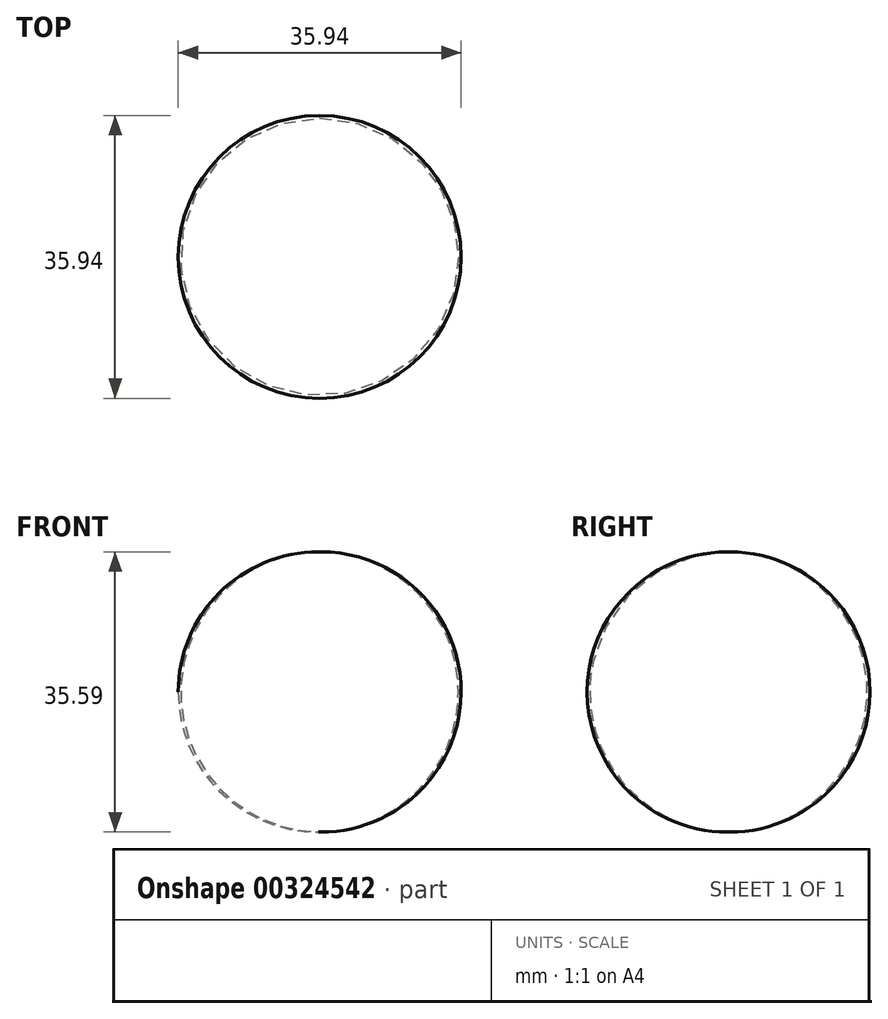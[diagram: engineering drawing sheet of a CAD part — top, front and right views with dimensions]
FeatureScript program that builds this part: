
annotation { "Feature Type Name" : "Feature", "Feature Type Description" : "" }
export const myFeature = defineFeature(function(context is Context, id is Id, definition is map)
    precondition{}
    {
        {
            var Q0;
            Q0=qCreatedBy(makeId("Front.planeOp"),FACE);
            var sketch = newSketch(context, id + "F0", { "sketchPlane" : qUnion([Q0])});
            skArc(sketch, "E0", {"start": v(0, -35.6) * mm, "mid": v(17.63, -17.8) * mm, "end": v(0, 0) * mm});
            skLineSegment(sketch, "E1", {"start": v(0, 0) * mm, "end": v(0, -35.6) * mm});
            skLineSegment(sketch, "E2", {"start": v(0, -59.1) * mm, "end": v(0, 28.13) * mm, "construction": true});
            skSolve(sketch);
        }
        {
            var Q0;
            Q0=makeQuery(id+"F0.imprint","IMPRINT",FACE,{"disambiguationData":[TD([[makeQuery(id+"F0.imprint","IMPRINT",EDGE,{"derivedFrom":sQuery(id+"F0.wireOp",EDGE,"E0")}),1.0]])]});
            var Q1;
            Q1=sQuery(id+"F0.wireOp",EDGE,"E2");
            revolve(context, id + "F1", {"entities" : qUnion([Q0]), "axis" : qUnion([Q1]), "revolveType" : RevolveType.FULL});
        }
    });
